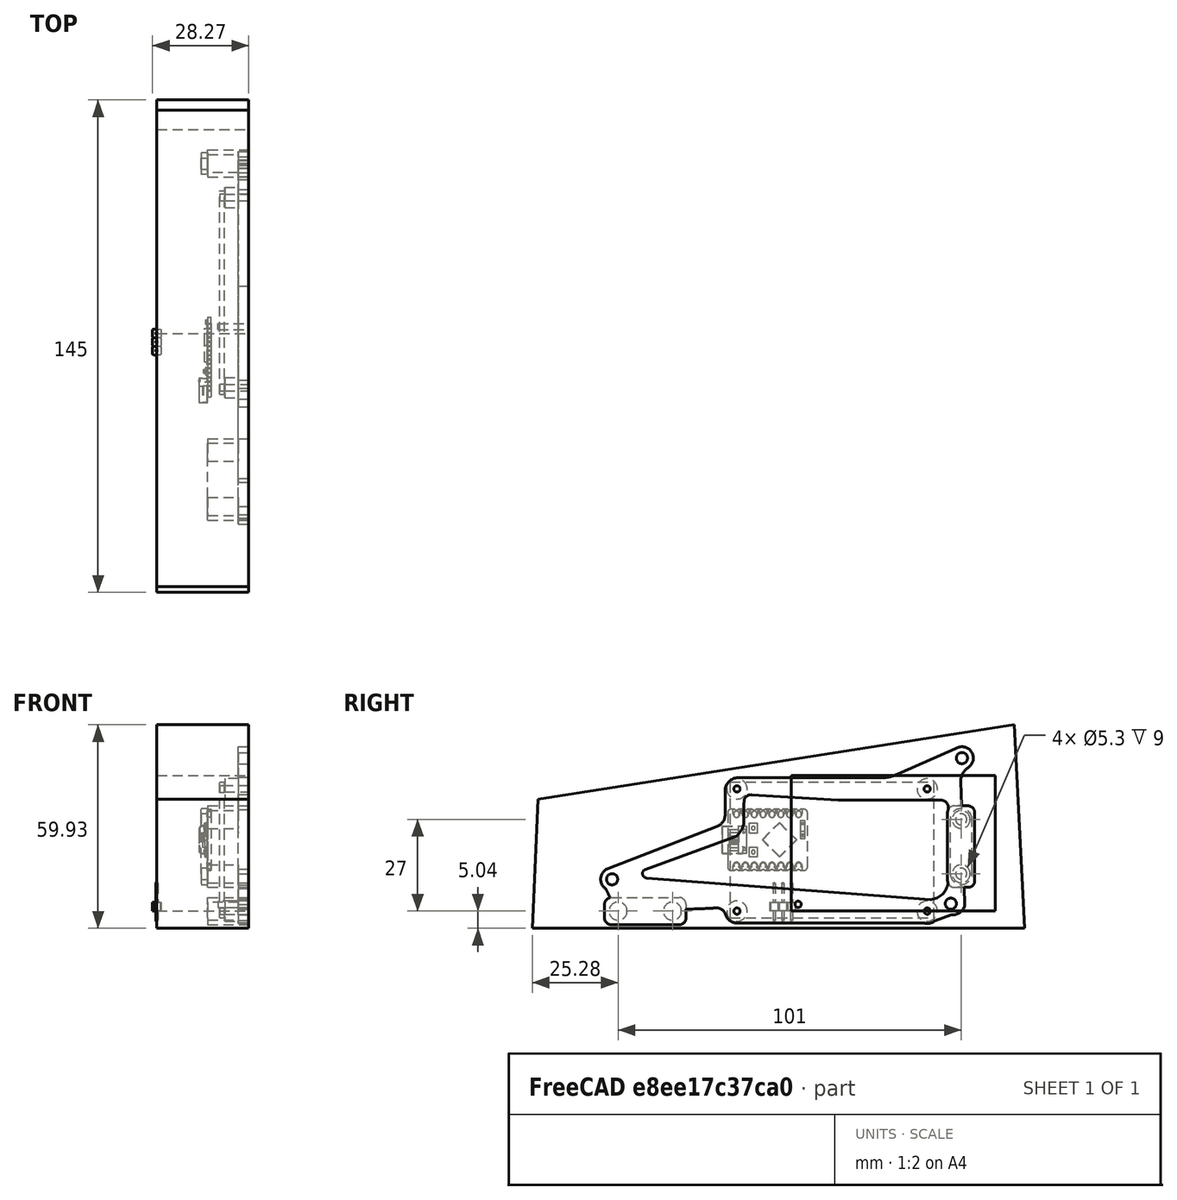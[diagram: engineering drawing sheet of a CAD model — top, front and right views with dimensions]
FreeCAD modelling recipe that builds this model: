
FCSTD DOCUMENT  (FreeCAD 1.0R39109 (Git))
Label: lamidi
License: All rights reserved
LicenseURL: https://en.wikipedia.org/wiki/All_rights_reserved
objects: Part::FeaturePython×10, Part::Feature×6, Part::MultiFuse×5, Sketcher::SketchObject×4, Part::Extrusion×4, Part::Cylinder×4, Part::Box×3, Part::Cut×3, App::Part×2, Mesh::Feature×1, Part::Fillet×1
note: 44 computed .brp shape members not serialized (recipe doc carries the construction recipe); baked Part::Feature solids carry a one-line shape summary decoded from their .brp

FEATURE [Part::Box] Box  label="inner001"
  AttacherType = Attacher::AttachEngine3D
  Height = 40
  Length = 27
  Width = 60
FEATURE [Part::Box] Box001  label="board001"
  AttacherType = Attacher::AttachEngine3D
  Height = 40
  Length = 1.4
  Width = 60
FEATURE [Sketcher::SketchObject] Sketch  label="holesSketch001"
  ArcFitTolerance = 1e-06
  AttachmentSupport = -> [Box001]
  ExternalGeometry = -> [Box001]
  FullyConstrained = true
  MakeInternals = false
  MapMode = 5
  Placement = pos=(1.4,0,0) rot=(0.57735,0.57735,0.57735;2.0944rad)
  sketch-geometry (14):
    g0: LineSegment [constr] StartX=2 StartY=38 StartZ=0 EndX=2 EndY=2 EndZ=0
    g1: LineSegment [constr] StartX=2 StartY=2 StartZ=0 EndX=58 EndY=2 EndZ=0
    g2: LineSegment [constr] StartX=58 StartY=2 StartZ=0 EndX=58 EndY=38 EndZ=0
    g3: LineSegment [constr] StartX=58 StartY=38 StartZ=0 EndX=2 EndY=38 EndZ=0
    g4: Circle CenterX=2 CenterY=38 CenterZ=0 NormalX=0 NormalY=0 NormalZ=1 AngleXU=0 Radius=1
    g5: Circle CenterX=58 CenterY=38 CenterZ=0 NormalX=0 NormalY=0 NormalZ=1 AngleXU=0 Radius=1
    g6: Circle CenterX=58 CenterY=2 CenterZ=0 NormalX=0 NormalY=0 NormalZ=1 AngleXU=0 Radius=1
    g7: Circle CenterX=2 CenterY=2 CenterZ=0 NormalX=0 NormalY=0 NormalZ=1 AngleXU=0 Radius=1
    g8: LineSegment [constr] StartX=2 StartY=38 StartZ=0 EndX=2 EndY=40 EndZ=0
    g9: LineSegment [constr] StartX=2 StartY=38 StartZ=0 EndX=0 EndY=38 EndZ=0
    g10: LineSegment [constr] StartX=58 StartY=38 StartZ=0 EndX=58 EndY=40 EndZ=0
    g11: LineSegment [constr] StartX=58 StartY=38 StartZ=0 EndX=60 EndY=38 EndZ=0
    g12: LineSegment [constr] StartX=58 StartY=2 StartZ=0 EndX=60 EndY=2 EndZ=0
    g13: LineSegment [constr] StartX=58 StartY=2 StartZ=0 EndX=58 EndY=0 EndZ=0
  constraints (38):
    c: Coincident(g0,g1)
    c: Coincident(g1,g2)
    c: Coincident(g2,g3)
    c: Coincident(g3,g0)
    c: Vertical(g0)
    c: Vertical(g2)
    c: Horizontal(g1)
    c: Horizontal(g3)
    c: Coincident(g4,g0)
    c: Coincident(g5,g2)
    c: Coincident(g6,g1)
    c: Coincident(g7,g0)
    c: Diameter(g4) = 2
    c: Diameter(g5) = 2
    c: Diameter(g7) = 2
    c: Diameter(g6) = 2
    c: Coincident(g8,g0)
    c: PointOnObject(g8,g-3)
    c: Vertical(g8)
    c: Coincident(g9,g0)
    c: PointOnObject(g9,g-2)
    c: Horizontal(g9)
    c: DistanceY(g8,g8) = 2
    c: DistanceX(g9,g9) = 2
    c: Coincident(g10,g2)
    c: PointOnObject(g10,g-3)
    c: Vertical(g10)
    c: Coincident(g11,g2)
    c: PointOnObject(g11,g-4)
    c: Horizontal(g11)
    c: Coincident(g12,g1)
    c: PointOnObject(g12,g-4)
    c: Horizontal(g12)
    c: Coincident(g13,g1)
    c: PointOnObject(g13,g-1)
    c: Vertical(g13)
    c: DistanceX(g12,g12) = 2
    c: DistanceY(g13,g13) = 2
FEATURE [Part::Extrusion] Extrude
  Base = -> Sketch
  Dir = (1,0,0)
  DirMode = 2
  FaceMakerClass = Part::FaceMakerBullseye
  FaceMakerMode = 3
  LengthFwd = -1.4
  LengthRev = 0
  Solid = true
  Symmetric = false
FEATURE [Part::Cut] Cut  label="board002"
  Base = -> Box001
  Placement = pos=(18.5,-18,-2) rot=(0,0,1;0rad)
  Refine = true
  Tool = -> Extrude
FEATURE [Part::Cylinder] Cylinder  label="hole001"
  Angle = 360
  AttacherType = Attacher::AttachEngine3D
  FirstAngle = 0
  Height = 9
  Placement = pos=(27,2,2) rot=(0,1,0;4.71239rad)
  Radius = 0.92
  SecondAngle = 0
FEATURE [Sketcher::SketchObject] Sketch001  label="outerSketch001"
  ArcFitTolerance = 1e-06
  AttachmentSupport = -> [Box]
  FullyConstrained = false
  MakeInternals = false
  MapMode = 5
  Placement = pos=(27,0,0) rot=(0.57735,0.57735,0.57735;2.0944rad)
  sketch-geometry (4):
    g0: LineSegment StartX=-76.2781 StartY=-5.03701 StartZ=0 EndX=68.7219 EndY=-5.03701 EndZ=0
    g1: LineSegment StartX=68.7219 StartY=-5.03701 StartZ=0 EndX=65.69 EndY=54.8863 EndZ=0
    g2: LineSegment StartX=65.69 StartY=54.8863 StartZ=0 EndX=-74.6016 EndY=32.926 EndZ=0
    g3: LineSegment StartX=-74.6016 StartY=32.926 StartZ=0 EndX=-76.2781 EndY=-5.03701 EndZ=0
  constraints (10):
    c: Horizontal(g0)
    c: Coincident(g0,g1)
    c: Coincident(g1,g2)
    c: Coincident(g2,g3)
    c: Coincident(g3,g0)
    c: DistanceX(g0,g0) = 145
    c: Distance(g1) = 60
    c: Distance(g3) = 38
    c: Distance(g2) = 142
    c: Angle(g2,g1) = 1.46608
FEATURE [Part::Extrusion] Extrude001  label="outerExtrude001"
  Base = -> Sketch001
  Dir = (1,0,0)
  DirMode = 2
  FaceMakerClass = Part::FaceMakerBullseye
  FaceMakerMode = 3
  LengthFwd = -27
  LengthRev = 0
  Solid = true
  Symmetric = false
FEATURE [Part::Cylinder] Cylinder001  label="attach001"
  Angle = 360
  AttacherType = Attacher::AttachEngine3D
  FirstAngle = 0
  Height = 7
  Placement = pos=(27,40,6e-15) rot=(0,1,0;4.71239rad)
  Radius = 3
  SecondAngle = 0
FEATURE [Part::FeaturePython] Clone  label="attach002"  # Draft clone (typed FeaturePython)
  AttacherType = Attacher::AttachEngine3D
  Fuse = false
  Objects = -> [Cylinder001]
  Placement = pos=(27,40,36) rot=(0,1,0;4.71239rad)
  Scale = (1,1,1)
FEATURE [Part::FeaturePython] Clone001  label="attach003"  # Draft clone (typed FeaturePython)
  AttacherType = Attacher::AttachEngine3D
  Fuse = false
  Objects = -> [Clone]
  Placement = pos=(27,-16,6e-15) rot=(0,1,0;4.71239rad)
  Scale = (1,1,1)
FEATURE [Part::FeaturePython] Clone002  label="attach004"  # Draft clone (typed FeaturePython)
  AttacherType = Attacher::AttachEngine3D
  Fuse = false
  Objects = -> [Clone001]
  Placement = pos=(27,-16,36) rot=(0,1,0;4.71239rad)
  Scale = (1,1,1)
FEATURE [Part::Cylinder] Cylinder002  label="hole002"
  Angle = 360
  AttacherType = Attacher::AttachEngine3D
  FirstAngle = 0
  Height = 7
  Placement = pos=(27,-16,0) rot=(0,1,0;4.71239rad)
  Radius = 0.925
  SecondAngle = 0
FEATURE [Part::FeaturePython] Clone003  label="hole003"  # Draft clone (typed FeaturePython)
  AttacherType = Attacher::AttachEngine3D
  Fuse = false
  Objects = -> [Cylinder002]
  Placement = pos=(27,-16,36) rot=(0,1,0;4.71239rad)
  Scale = (1,1,1)
FEATURE [Part::FeaturePython] Clone004  label="hole004"  # Draft clone (typed FeaturePython)
  AttacherType = Attacher::AttachEngine3D
  Fuse = false
  Objects = -> [Clone003]
  Placement = pos=(27,40,0) rot=(0,1,0;4.71239rad)
  Scale = (1,1,1)
FEATURE [Part::FeaturePython] Clone005  label="hole005"  # Draft clone (typed FeaturePython)
  AttacherType = Attacher::AttachEngine3D
  Fuse = false
  Objects = -> [Clone004]
  Placement = pos=(27,40,36) rot=(0,1,0;4.71239rad)
  Scale = (1,1,1)
FEATURE [Sketcher::SketchObject] Sketch002  label="bracketSketch001"
  ArcFitTolerance = 1e-06
  AttachmentSupport = -> [Extrude001]
  ExternalGeometry = -> [Extrude001,Clone003,Cylinder002,Clone005,Clone004]
  FullyConstrained = false
  MakeInternals = false
  MapMode = 5
  Placement = pos=(27,0,0) rot=(0.57735,0.57735,0.57735;2.0944rad)
  sketch-geometry (67):
    g0: Circle CenterX=-52.7746 CenterY=9.37299 CenterZ=0 NormalX=0 NormalY=0 NormalZ=1 AngleXU=0 Radius=1.65
    g1: Circle CenterX=50.2206 CenterY=45.0597 CenterZ=0 NormalX=0 NormalY=0 NormalZ=1 AngleXU=0 Radius=1.65
    g2: Circle CenterX=46.9666 CenterY=2.18299 CenterZ=0 NormalX=0 NormalY=0 NormalZ=1 AngleXU=0 Radius=1.65
    g3: LineSegment [constr] StartX=50.2206 StartY=45.0597 StartZ=0 EndX=46.9666 EndY=2.18299 EndZ=0
    g4: LineSegment [constr] StartX=46.9666 StartY=2.18299 StartZ=0 EndX=-52.7746 EndY=9.37299 EndZ=0
    g5: LineSegment [constr] StartX=-52.7746 StartY=9.37299 StartZ=0 EndX=-52.7746 EndY=-5.03701 EndZ=0
    g6: LineSegment [constr] StartX=46.9666 StartY=2.18299 StartZ=0 EndX=46.9666 EndY=-5.03701 EndZ=0
    g7: LineSegment [constr] StartX=46.9666 StartY=2.18299 StartZ=0 EndX=68.3566 EndY=2.18299 EndZ=0
    g8: ArcOfCircle CenterX=-52.7746 CenterY=9.37299 CenterZ=0 NormalX=0 NormalY=0 NormalZ=1 AngleXU=0 Radius=3.36177 StartAngle=1.94036 EndAngle=4.12018
    g9: ArcOfCircle CenterX=50.2206 CenterY=45.0597 CenterZ=0 NormalX=0 NormalY=0 NormalZ=1 AngleXU=0 Radius=3.36177 StartAngle=5.28632 EndAngle=8.11739
    g10: LineSegment StartX=-53.9889 StartY=12.5078 StartZ=0 EndX=-21.8408 EndY=24.9606 EndZ=0
    g11: LineSegment StartX=49.8854 StartY=38.1101 StartZ=0 EndX=51.0551 EndY=1.83276 EndZ=0
    g12: LineSegment StartX=-42.6099 StartY=9.74641 StartZ=0 EndX=41.0083 EndY=3.39546 EndZ=0
    g13: ArcOfCircle CenterX=47.4568 CenterY=2.5341 CenterZ=0 NormalX=0 NormalY=0 NormalZ=1 AngleXU=0 Radius=3.66597 StartAngle=4.62415 EndAngle=6.09069
    g14: ArcOfCircle CenterX=-42.5107 CenterY=11.0523 CenterZ=0 NormalX=0 NormalY=0 NormalZ=1 AngleXU=0 Radius=1.30969 StartAngle=1.87408 EndAngle=4.63658
    g15: GeomPoint [constr] X=46.5532 Y=2.97432 Z=0
    g16: LineSegment [constr] StartX=-42.5107 StartY=11.0523 StartZ=0 EndX=-42.9148 EndY=5.7769 EndZ=0
    g17: LineSegment [constr] StartX=-40.9447 StartY=13.0486 StartZ=0 EndX=-42.4644 EndY=16.9719 EndZ=0
    g18: LineSegment StartX=-19.5055 StartY=35.3516 StartZ=0 EndX=-19.5055 EndY=28.3696 EndZ=0
    g19: LineSegment StartX=26.4055 StartY=39.292 StartZ=0 EndX=-15.5651 EndY=39.292 EndZ=0
    g20: LineSegment StartX=-13.9433 StartY=31.7041 StartZ=0 EndX=-13.9433 EndY=26.6158 EndZ=0
    g21: LineSegment StartX=46.1884 StartY=9.05978 StartZ=0 EndX=46.1884 EndY=30.6503 EndZ=0
    g22: LineSegment StartX=44.1892 StartY=32.6496 StartZ=0 EndX=13.8121 EndY=32.6496 EndZ=0
    g23: LineSegment [constr] StartX=-19.5055 StartY=39.292 StartZ=0 EndX=-13.9433 EndY=34.4258 EndZ=0
    g24: ArcOfCircle CenterX=-15.5651 CenterY=35.3516 CenterZ=0 NormalX=0 NormalY=0 NormalZ=1 AngleXU=0 Radius=3.94046 StartAngle=1.5708 EndAngle=3.14159
    g25: GeomPoint [constr] X=-19.5055 Y=39.292 Z=0
    g26: GeomPoint [constr] X=44.8538 Y=-5.03701 Z=0
    g27: GeomPoint [constr] X=-15.8688 Y=-5.03701 Z=0
    g28: ArcOfCircle CenterX=-7.55072 CenterY=31.7041 CenterZ=0 NormalX=0 NormalY=0 NormalZ=1 AngleXU=0 Radius=6.3926 StartAngle=3.02634 EndAngle=3.14159
    g29: GeomPoint [constr] X=-13.9433 Y=34.4258 Z=0
    g30: GeomPoint [constr] X=-15.8823 Y=2.56735 Z=0
    g31: ArcOfCircle CenterX=44.1892 CenterY=30.6503 CenterZ=0 NormalX=0 NormalY=0 NormalZ=1 AngleXU=0 Radius=1.99928 StartAngle=0 EndAngle=1.5708
    g32: ArcOfCircle CenterX=40.5015 CenterY=9.05978 CenterZ=0 NormalX=0 NormalY=0 NormalZ=1 AngleXU=0 Radius=5.68695 StartAngle=4.80162 EndAngle=6.28319
    g33: GeomPoint [constr] X=46.1884 Y=2.23908 Z=0
    g34: LineSegment StartX=13.8121 StartY=32.6496 StartZ=0 EndX=-11.6946 EndY=34.2819 EndZ=0
    g35: LineSegment StartX=31.1597 StartY=40.293 StartZ=0 EndX=49.3453 EndY=48.3055 EndZ=0
    g36: LineSegment StartX=-42.9019 StartY=12.3023 StartZ=0 EndX=-16.9428 EndY=21.7315 EndZ=0
    g37: LineSegment StartX=-14.9539 StartY=23.4866 StartZ=0 EndX=-15.3532 EndY=22.933 EndZ=0
    g38: ArcOfCircle CenterX=-16 CenterY=0 CenterZ=0 NormalX=0 NormalY=0 NormalZ=1 AngleXU=0 Radius=3.51632 StartAngle=3.44567 EndAngle=4.63298
    g39: ArcOfCircle CenterX=40 CenterY=0 CenterZ=0 NormalX=0 NormalY=0 NormalZ=1 AngleXU=0 Radius=3.64954 StartAngle=4.43024 EndAngle=5.37731
    g40: LineSegment StartX=-16.279 StartY=-3.50524 StartZ=0 EndX=38.9839 EndY=-3.50524 EndZ=0
    g41: LineSegment StartX=47.1338 StartY=-1.1176 StartZ=0 EndX=42.2518 EndY=-2.87207 EndZ=0
    g42: ArcOfCircle CenterX=-19.2932 CenterY=26.6158 CenterZ=0 NormalX=0 NormalY=0 NormalZ=1 AngleXU=0 Radius=5.34989 StartAngle=5.65841 EndAngle=6.28319
    g43: GeomPoint [constr] X=-13.9433 Y=24.888 Z=0
    g44: ArcOfCircle CenterX=-18.0983 CenterY=24.9126 CenterZ=0 NormalX=0 NormalY=0 NormalZ=1 AngleXU=0 Radius=3.38447 StartAngle=5.0608 EndAngle=5.65841
    g45: GeomPoint [constr] X=-15.9629 Y=22.0874 Z=0
    g46: ArcOfCircle CenterX=26.4055 CenterY=51.0833 CenterZ=0 NormalX=0 NormalY=0 NormalZ=1 AngleXU=0 Radius=11.7913 StartAngle=4.71239 EndAngle=5.1274
    g47: GeomPoint [constr] X=28.888 Y=39.292 Z=0
    g48: ArcOfCircle CenterX=-23.1613 CenterY=28.3696 CenterZ=0 NormalX=0 NormalY=0 NormalZ=1 AngleXU=0 Radius=3.65579 StartAngle=5.08195 EndAngle=6.28319
    g49: GeomPoint [constr] X=-19.5055 Y=25.8652 Z=0
    g50: ArcOfCircle CenterX=54.6152 CenterY=38.2626 CenterZ=0 NormalX=0 NormalY=0 NormalZ=1 AngleXU=0 Radius=4.73226 StartAngle=2.14473 EndAngle=3.17382
    g51: ArcOfCircle CenterX=-11.8279 CenterY=32.1993 CenterZ=0 NormalX=0 NormalY=0 NormalZ=1 AngleXU=0 Radius=2.08686 StartAngle=1.50689 EndAngle=3.02634
    g52: ArcOfCircle CenterX=-22.1065 CenterY=-1.91625 CenterZ=0 NormalX=0 NormalY=0 NormalZ=1 AngleXU=0 Radius=2.88377 StartAngle=0.304073 EndAngle=1.44586
    g53-g60: Circle [constr] x8 (B-spline internal-alignment scaffolding for g61; pole/knot coordinates omitted)
    g61: BSplineCurve PolesCount=8 KnotsCount=6 Degree=3 IsPeriodic=0
    g62-g66: GeomPoint [constr] x5 (B-spline internal-alignment scaffolding for g61; pole/knot coordinates omitted)
  constraints (92):
    c: Diameter(g0) = 3.3
    c: Diameter(g1) = 3.3
    c: Diameter(g2) = 3.3
    c: Coincident(g3,g1)
    c: Coincident(g3,g2)
    c: Coincident(g4,g2)
    c: Coincident(g4,g0)
    c: Distance(g4) = 100
    c: Distance(g3) = 43
    c: Coincident(g5,g0)
    c: PointOnObject(g5,g-3)
    c: Coincident(g6,g2)
    c: PointOnObject(g6,g-3)
    c: Vertical(g6)
    c: DistanceY(g5,g5) = 14.41
    c: DistanceY(g6,g6) = 7.22
    c: Angle(g-3,g5) = 1.5708
    c: Coincident(g7,g2)
    c: Horizontal(g7)
    c: DistanceX(g7,g7) = 21.39
    c: PointOnObject(g7,g-4)
    c: Tangent(g8,g10) = 1.5708
    c: Coincident(g9,g35) = 1.5708
    c: Equal(g8,g9)
    c: Coincident(g8,g0)
    c: Coincident(g9,g1)
    c: Coincident(g13,g11) = 1.5708
    c: Tangent(g12,g14) = -1.5708
    c: PointOnObject(g15,g12)
    c: Coincident(g16,g14)
    c: PointOnObject(g17,g10)
    c: Angle(g17,g10) = 1.5708
    c: Vertical(g18)
    c: Horizontal(g19)
    c: PointOnObject(g26,g-3)
    c: Vertical(g20)
    c: Vertical(g21)
    c: Horizontal(g22)
    c: PointOnObject(g33,g4)
    c: Coincident(g23,g25)
    c: Coincident(g23,g29)
    c: PointOnObject(g25,g19)
    c: PointOnObject(g25,g18)
    c: Tangent(g19,g24) = -1.5708
    c: Tangent(g18,g24) = -1.5708
    c: PointOnObject(g29,g34)
    c: PointOnObject(g29,g20)
    c: Tangent(g20,g28) = -1.5708
    c: Tangent(g22,g31) = -1.5708
    c: Tangent(g21,g31) = -1.5708
    c: PointOnObject(g33,g21)
    c: Tangent(g21,g32) = -1.5708
    c: PointOnObject(g34,g35)
    c: Coincident(g12,g32)
    c: Coincident(g34,g22)
    c: Coincident(g36,g14)
    c: Coincident(g38,g-6)
    c: Coincident(g39,g-8)
    c: Coincident(g40,g38)
    c: Coincident(g40,g39)
    c: Horizontal(g40)
    c: Coincident(g41,g13)
    c: Coincident(g41,g39)
    c: PointOnObject(g43,g20)
    c: PointOnObject(g43,g37)
    c: Tangent(g20,g42) = 1.5708
    c: Tangent(g37,g42) = 1.5708
    c: PointOnObject(g45,g36)
    c: PointOnObject(g45,g37)
    c: Tangent(g36,g44) = -1.5708
    c: Tangent(g37,g44) = 1.5708
    c: PointOnObject(g47,g19)
    c: PointOnObject(g47,g35)
    c: Tangent(g19,g46) = 1.5708
    c: Tangent(g35,g46) = -1.5708
    c: PointOnObject(g49,g18)
    c: PointOnObject(g49,g10)
    c: Tangent(g18,g48) = 1.5708
    c: Tangent(g10,g48) = -1.5708
    c: Tangent(g9,g50) = 1.5708
    c: Tangent(g11,g50) = -1.5708
    c: Tangent(g34,g51) = -1.5708
    c: Tangent(g28,g51) = -1.5708
    c: Tangent(g38,g52) = 1.5708
    c: Weight(g53) = 1
    c: Equal(g53, g54-g60) x7
    c: InternalAlignment(g53-g60 -> g61) x8
    c: InternalAlignment(g62-g66 -> g61) x5
    c: Coincident(g53,g8)
    c: PointOnObject(g55,g54)
    c: Coincident(g59,g52)
    c: Coincident(g60,g52)
FEATURE [Part::Extrusion] Extrude002  label="bracketExtrude001"
  Base = -> Sketch002
  Dir = (1,0,0)
  DirMode = 2
  FaceMakerClass = Part::FaceMakerBullseye
  FaceMakerMode = 3
  LengthFwd = -3
  LengthRev = 0
  Solid = true
  Symmetric = false
FEATURE [Part::MultiFuse] Fusion  label="holesFusion001"
  Refine = true
  Shapes = -> [Cylinder002,Clone003,Clone004,Clone005]
FEATURE [Part::MultiFuse] Fusion001
  Refine = true
  Shapes = -> [Extrude002,Clone002,Clone001,Clone,Cylinder001]
FEATURE [Part::Cut] Cut001  label="fullbracket001"
  Base = -> Fusion001
  Refine = true
  Tool = -> Fusion
FEATURE [Part::Feature] Part__Feature  label="esp32 s3"
  Placement = pos=(16,-7,21) rot=(0.57735,0.57735,-0.57735;2.0944rad)
  shape: bbox 3.595 x 25.1 x 18 mm, 225 faces (baked)
FEATURE [Part::Feature] Part__Feature001  label="1x1_Pin_Header_2.54mm"
  Placement = pos=(0,0,-3) rot=(0,0,1;0rad)
  shape: bbox 2.54 x 2.54 x 11.5 mm, 28 faces (baked)
FEATURE [Part::Feature] Part__Feature002  label="1x1_Pin_Header_2.54mm001"
  Placement = pos=(0,-2.54,-3) rot=(0,0,1;0rad)
  shape: bbox 2.54 x 2.54 x 11.5 mm, 28 faces (baked)
FEATURE [Part::Feature] Part__Feature003  label="1x1_Pin_Header_2.54mm002"
  Placement = pos=(0,-5.08,-3) rot=(0,0,1;0rad)
  shape: bbox 2.54 x 2.54 x 11.5 mm, 28 faces (baked)
FEATURE [App::Part] _x1_Pin_Header_2_54mm  label="3x1_Pin_Header_2.54mm"
  Group = -> [Part__Feature001,Part__Feature002,Part__Feature003]
  Origin = -> Origin
  Placement = pos=(18.5,36,31) rot=(0,1,0;4.71239rad)
FEATURE [Part::Feature] Part__Feature004  label="1x1_Pin_Header_2.54mm003"
  Placement = pos=(0,0,-3) rot=(0,0,1;0rad)
  shape: bbox 2.54 x 2.54 x 11.5 mm, 28 faces (baked)
FEATURE [Part::Feature] Part__Feature005  label="1x1_Pin_Header_2.54mm004"
  Placement = pos=(0,-2.54,-3) rot=(0,0,1;0rad)
  shape: bbox 2.54 x 2.54 x 11.5 mm, 28 faces (baked)
FEATURE [App::Part] _x1_Pin_Header_2_54mm001  label="2x1_Pin_Header_2.54mm"
  Group = -> [Part__Feature004,Part__Feature005]
  Origin = -> Origin001
  Placement = pos=(18.5,-16,7) rot=(0.57735,0.57735,-0.57735;4.18879rad)
FEATURE [Mesh::Feature] usb_c_connector  label="usb-c_connector"
  Placement = pos=(71.5,-40,113.3) rot=(0.57735,-0.57735,-0.57735;4.18879rad)
FEATURE [Part::Box] Box002  label="tie001"
  AttacherType = Attacher::AttachEngine3D
  Height = 8
  Length = 12
  Placement = pos=(15,-55,-1) rot=(0,0,1;0rad)
  Width = 24
FEATURE [Part::Cylinder] Cylinder003  label="insert001"
  Angle = 360
  AttacherType = Attacher::AttachEngine3D
  FirstAngle = 0
  Height = 9
  Placement = pos=(24,-35,3) rot=(0,1,0;4.71239rad)
  Radius = 2.65
  SecondAngle = 0
FEATURE [Part::FeaturePython] Clone006  label="insert002"  # Draft clone (typed FeaturePython)
  AttacherType = Attacher::AttachEngine3D
  Fuse = false
  Objects = -> [Cylinder003]
  Placement = pos=(24,-51,3) rot=(0,1,0;4.71239rad)
  Scale = (1,1,1)
FEATURE [Part::Fillet] Fillet  label="tieFillet001"
  Base = -> Box002
  EdgeLinks = -> Box002 [Edge9,Edge10,Edge11,Edge12]
  Edges = 4 edges r=2: [Edge9,Edge10,Edge11,Edge12]
  Placement = pos=(0,0,-3) rot=(0,0,1;0rad)
FEATURE [Sketcher::SketchObject] Sketch003
  ArcFitTolerance = 1e-06
  AttachmentSupport = -> [Fillet]
  FullyConstrained = false
  MakeInternals = false
  MapMode = 5
  Placement = pos=(15,0,-3) rot=(0.57735,-0.57735,-0.57735;2.0944rad)
  sketch-geometry (7):
    g0: ArcOfCircle CenterX=35.033 CenterY=3.01566 CenterZ=0 NormalX=0 NormalY=0 NormalZ=1 AngleXU=0 Radius=3.19704 StartAngle=1.5708 EndAngle=4.71239
    g1: ArcOfCircle CenterX=51.033 CenterY=3.01566 CenterZ=0 NormalX=0 NormalY=0 NormalZ=1 AngleXU=0 Radius=3.19704 StartAngle=4.71239 EndAngle=7.85398
    g2: LineSegment StartX=35.033 StartY=6.2127 StartZ=0 EndX=51.033 EndY=6.2127 EndZ=0
    g3: LineSegment StartX=35.033 StartY=-0.181372 StartZ=0 EndX=51.033 EndY=-0.181372 EndZ=0
    g4: Circle CenterX=35.033 CenterY=3.01566 CenterZ=0 NormalX=0 NormalY=0 NormalZ=1 AngleXU=0 Radius=1.65
    g5: Circle CenterX=51.033 CenterY=3.01566 CenterZ=0 NormalX=0 NormalY=0 NormalZ=1 AngleXU=0 Radius=1.65
    g6: LineSegment [constr] StartX=35.033 StartY=3.01566 StartZ=0 EndX=51.033 EndY=3.01566 EndZ=0
  constraints (13):
    c: Tangent(g0,g2) = 1.5708
    c: Tangent(g0,g3) = -1.5708
    c: Tangent(g1,g2) = 1.5708
    c: Tangent(g1,g3) = -1.5708
    c: Equal(g0,g1)
    c: Horizontal(g3)
    c: Coincident(g4,g0)
    c: Coincident(g5,g1)
    c: Diameter(g4) = 3.3
    c: Diameter(g5) = 3.3
    c: Coincident(g6,g0)
    c: Coincident(g6,g1)
    c: DistanceX(g6,g6) = 16
FEATURE [Part::Extrusion] Extrude003  label="tieLidExtrude001"
  Base = -> Sketch003
  Dir = (-1,0,0)
  DirMode = 2
  FaceMakerClass = Part::FaceMakerBullseye
  FaceMakerMode = 3
  LengthFwd = 2
  LengthRev = 0
  Solid = true
  Symmetric = false
FEATURE [Part::MultiFuse] Fusion002  label="tieInserts001"
  Placement = pos=(0,0,-3) rot=(0,0,1;0rad)
  Refine = true
  Shapes = -> [Cylinder003,Clone006]
FEATURE [Part::FeaturePython] Clone008  label="tieLidExtrude002"  # Draft clone (typed FeaturePython)
  AttacherType = Attacher::AttachEngine3D
  Fuse = false
  Objects = -> [Extrude003]
  Placement = pos=(0,50,-24) rot=(1,0,0;4.71239rad)
  Scale = (1,1,1)
FEATURE [Part::FeaturePython] Clone009  label="tieInserts002"  # Draft clone (typed FeaturePython)
  AttacherType = Attacher::AttachEngine3D
  Fuse = false
  Objects = -> [Fusion002]
  Placement = pos=(0,53,62) rot=(1,0,0;1.5708rad)
  Scale = (1,1,1)
FEATURE [Part::FeaturePython] Clone010  label="tieFillet002"  # Draft clone (typed FeaturePython)
  AttacherType = Attacher::AttachEngine3D
  Fuse = false
  Objects = -> [Fillet]
  Placement = pos=(0,53,62) rot=(1,0,0;1.5708rad)
  Scale = (1,1,1)
FEATURE [Part::MultiFuse] Fusion003  label="insertsFusion003"
  Refine = true
  Shapes = -> [Clone009,Fusion002]
FEATURE [Part::MultiFuse] Fusion004  label="fullBracket001"
  Refine = true
  Shapes = -> [Clone010,Fillet,Cut001]
FEATURE [Part::Cut] Cut002  label="fullbracket002"
  Base = -> Fusion004
  Refine = true
  Tool = -> Fusion003
